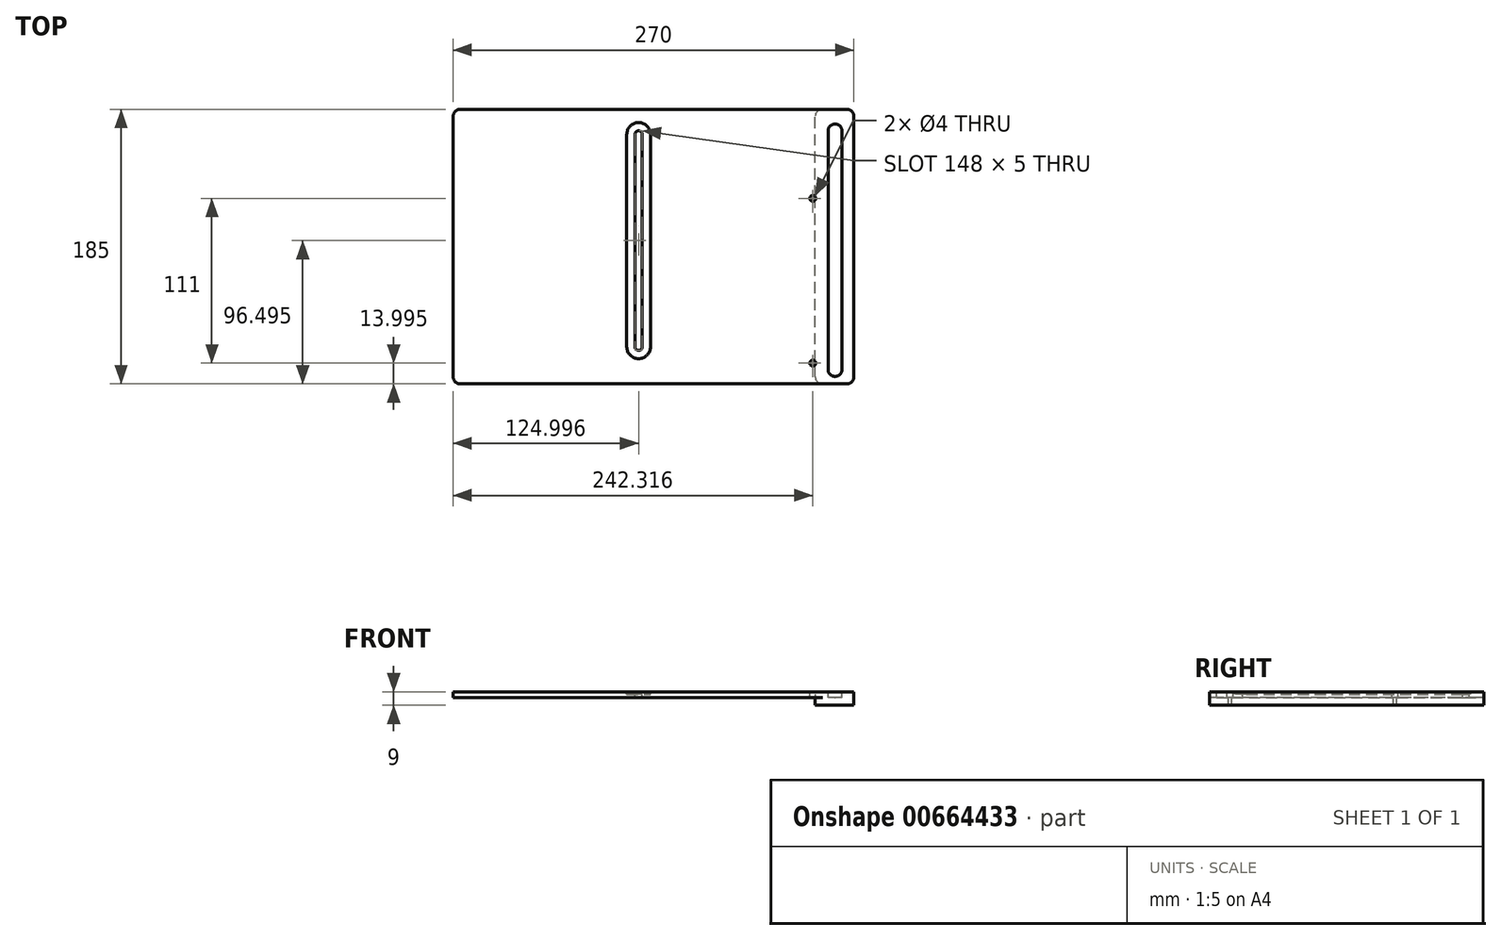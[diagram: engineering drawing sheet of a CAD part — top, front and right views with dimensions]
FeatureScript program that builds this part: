
annotation { "Feature Type Name" : "Feature", "Feature Type Description" : "" }
export const myFeature = defineFeature(function(context is Context, id is Id, definition is map)
    precondition{}
    {
        {
            var Q0;
            Q0=qCreatedBy(makeId("Top.planeOp"),FACE);
            var sketch = newSketch(context, id + "F0", { "sketchPlane" : qUnion([Q0])});
            skLineSegment(sketch, "E0.bottom", {"start": v(-79.13, 97.17) * mm, "end": v(170.87, 97.17) * mm});
            skLineSegment(sketch, "E0.top", {"start": v(-79.13, -87.83) * mm, "end": v(170.87, -87.83) * mm});
            skLineSegment(sketch, "E0.left", {"start": v(-79.13, 97.17) * mm, "end": v(-79.13, -87.83) * mm});
            skLineSegment(sketch, "E0.right", {"start": v(170.87, 97.17) * mm, "end": v(170.87, -87.83) * mm});
            skSolve(sketch);
        }
        {
            var Q0;
            Q0=makeQuery(id+"F0.imprint","IMPRINT",FACE,{"disambiguationData":[TD([[makeQuery(id+"F0.imprint","IMPRINT",EDGE,{"derivedFrom":sQuery(id+"F0.wireOp",EDGE,"E0.bottom")}),-1.0]])]});
            extrude(context, id + "F1", {"entities" : qUnion([Q0]), "depth" : 4 * mm, "offsetDistance" : 25 * mm});
        }
        {
            var Q0;
            Q0=makeQuery(id+"F1.opExtrude","CAP_FACE",FACE,{"disambiguationData":[OSD([sQuery(id+"F0.wireOp",EDGE,"E0.bottom"),sQuery(id+"F0.wireOp",EDGE,"E0.top"),sQuery(id+"F0.wireOp",EDGE,"E0.left"),sQuery(id+"F0.wireOp",EDGE,"E0.right")])],"isStart":false});
            var sketch = newSketch(context, id + "F2", { "sketchPlane" : qUnion([Q0])});
            skLineSegment(sketch, "E1", {"start": v(45.87, 97.17) * mm, "end": v(45.87, 72.17) * mm});
            skArc(sketch, "E2", {"start": v(53.87, 80.17) * mm, "mid": v(45.87, 88.17) * mm, "end": v(37.87, 80.17) * mm});
            skArc(sketch, "E3", {"start": v(37.87, -62.83) * mm, "mid": v(45.87, -70.83) * mm, "end": v(53.87, -62.83) * mm});
            skLineSegment(sketch, "E4", {"start": v(37.87, 80.17) * mm, "end": v(37.87, -62.83) * mm});
            skLineSegment(sketch, "E5", {"start": v(53.87, -62.83) * mm, "end": v(53.87, 80.17) * mm});
            skLineSegment(sketch, "E6.trimOffspring", {"start": v(45.87, -54.83) * mm, "end": v(45.87, -87.83) * mm});
            skSolve(sketch);
        }
        {
            var Q0;
            {var subQ3=sQuery(id+"F2.wireOp",EDGE,"E4");Q0=makeQuery(id+"F2.imprint","IMPRINT",FACE,{"disambiguationData":[TD([[makeQuery(id+"F2.imprint","IMPRINT",EDGE,{"derivedFrom":subQ3}),1.0]])]});}
            var Q1;
            {var subQ0=sQuery(id+"F2.wireOp",EDGE,"E6.trimOffspring");var subQ1=sQuery(id+"F2.wireOp",EDGE,"E3");var subQ2=makeQuery(id+"F2.imprint","INTERSECT",VERTEX,{"disambiguationData":[OD(0.0)],"derivedFrom":[subQ1,subQ0]});Q1=makeQuery(id+"F2.imprint","IMPRINT",FACE,{"disambiguationData":[TD([[makeQuery(id+"F2.imprint","IMPRINT",EDGE,{"disambiguationData":[TD([[subQ2,-1.0]])],"derivedFrom":subQ1}),1.0]])]});}
            extrude(context, id + "F3", {"entities" : qUnion([Q0, Q1]), "operationType" : NewBodyOperationType.REMOVE, "oppositeDirection" : true, "depth" : 1.5 * mm, "offsetDistance" : 25 * mm});
        }
        {
            var Q0;
            Q0=makeQuery(id+"F3.boolean.opBoolean","COPY",FACE,{"derivedFrom":makeQuery(id+"F3.opExtrude","CAP_FACE",FACE,{"disambiguationData":[OSD([sQuery(id+"F2.wireOp",EDGE,"E2"),sQuery(id+"F2.wireOp",EDGE,"E3"),sQuery(id+"F2.wireOp",EDGE,"E4"),sQuery(id+"F2.wireOp",EDGE,"E5")])],"isStart":false})});
            var sketch = newSketch(context, id + "F4", { "sketchPlane" : qUnion([Q0])});
            skArc(sketch, "E7", {"start": v(48.37, 80.17) * mm, "mid": v(45.87, 82.67) * mm, "end": v(43.37, 80.17) * mm});
            skArc(sketch, "E8", {"start": v(43.37, -62.83) * mm, "mid": v(45.87, -65.33) * mm, "end": v(48.37, -62.83) * mm});
            skLineSegment(sketch, "E9", {"start": v(48.37, 80.17) * mm, "end": v(48.37, -62.83) * mm});
            skLineSegment(sketch, "E10", {"start": v(43.37, 80.17) * mm, "end": v(43.37, -62.83) * mm});
            skArc(sketch, "E11.0", {"start": v(53.37, 80.17) * mm, "mid": v(45.87, 87.67) * mm, "end": v(38.37, 80.17) * mm});
            skLineSegment(sketch, "E11.1", {"start": v(53.37, 80.17) * mm, "end": v(53.37, -62.83) * mm});
            skArc(sketch, "E11.2", {"start": v(38.37, -62.83) * mm, "mid": v(45.87, -70.33) * mm, "end": v(53.37, -62.83) * mm});
            skSolve(sketch);
        }
        {
            var Q0;
            {var subQ3=sQuery(id+"F4.wireOp",EDGE,"E8");Q0=makeQuery(id+"F4.imprint","IMPRINT",FACE,{"disambiguationData":[TD([[makeQuery(id+"F4.imprint","IMPRINT",EDGE,{"derivedFrom":subQ3}),1.0]])]});}
            extrude(context, id + "F5", {"entities" : qUnion([Q0]), "operationType" : NewBodyOperationType.REMOVE, "oppositeDirection" : true, "depth" : 5 * mm, "offsetDistance" : 25 * mm});
        }
        {
            var Q0;
            Q0=makeQuery(id+"F1.opExtrude","CAP_FACE",FACE,{"disambiguationData":[OSD([sQuery(id+"F0.wireOp",EDGE,"E0.bottom"),sQuery(id+"F0.wireOp",EDGE,"E0.top"),sQuery(id+"F0.wireOp",EDGE,"E0.left"),sQuery(id+"F0.wireOp",EDGE,"E0.right")])],"isStart":false});
            var sketch = newSketch(context, id + "F6", { "sketchPlane" : qUnion([Q0])});
            skLineSegment(sketch, "E12", {"start": v(170.87, 37.17) * mm, "end": v(163.19, 37.17) * mm});
            skCircle(sketch, "E13", {"center": v(163.19, 37.17) * mm, "radius": 2 * mm});
            skCircle(sketch, "E14", {"center": v(163.19, -73.83) * mm, "radius": 2 * mm});
            skSolve(sketch);
        }
        {
            var Q0;
            Q0=makeQuery(id+"F6.imprint","IMPRINT",FACE,{"disambiguationData":[TD([[makeQuery(id+"F6.imprint","IMPRINT",EDGE,{"derivedFrom":sQuery(id+"F6.wireOp",EDGE,"E13")}),1.0]])]});
            var Q1;
            Q1=makeQuery(id+"F6.imprint","IMPRINT",FACE,{"disambiguationData":[TD([[makeQuery(id+"F6.imprint","IMPRINT",EDGE,{"derivedFrom":sQuery(id+"F6.wireOp",EDGE,"E14")}),1.0]])]});
            extrude(context, id + "F7", {"entities" : qUnion([Q0, Q1]), "operationType" : NewBodyOperationType.REMOVE, "oppositeDirection" : true, "depth" : 25 * mm, "offsetDistance" : 25 * mm});
        }
        {
            var Q0;
            Q0=makeQuery(id+"F1.opExtrude","SWEPT_FACE",FACE,{"disambiguationData":[OSD([sQuery(id+"F0.wireOp",EDGE,"E0.right")])]});
            extrude(context, id + "F8", {"entities" : qUnion([Q0]), "operationType" : NewBodyOperationType.ADD, "depth" : 20 * mm, "offsetDistance" : 25 * mm});
        }
        {
            var Q0;
            {var subQ0=sQuery(id+"F0.wireOp",EDGE,"E0.right");Q0=makeQuery(id+"F8.boolean.opBoolean","MERGE",FACE,{"derivedFrom":[makeQuery(id+"F1.opExtrude","CAP_FACE",FACE,{"disambiguationData":[OSD([sQuery(id+"F0.wireOp",EDGE,"E0.bottom"),sQuery(id+"F0.wireOp",EDGE,"E0.top"),sQuery(id+"F0.wireOp",EDGE,"E0.left"),subQ0])],"isStart":false}),makeQuery(id+"F8.opExtrude","SWEPT_FACE",FACE,{"disambiguationData":[OSD([subQ0]),TDD([makeQuery(id+"F1.opExtrude","CAP_EDGE",EDGE,{"disambiguationData":[OSD([subQ0])],"isStart":false})])]})]});}
            var sketch = newSketch(context, id + "F9", { "sketchPlane" : qUnion([Q0])});
            skLineSegment(sketch, "E15.bottom", {"start": v(178.07, 87.17) * mm, "end": v(178.37, 87.17) * mm});
            skLineSegment(sketch, "E15.top", {"start": v(178.07, -82.83) * mm, "end": v(178.37, -82.83) * mm});
            skLineSegment(sketch, "E15.left", {"start": v(173.57, 82.67) * mm, "end": v(173.57, -78.33) * mm});
            skLineSegment(sketch, "E15.right", {"start": v(182.87, 82.67) * mm, "end": v(182.87, -78.33) * mm});
            skPoint(sketch, "E16.visualSharp", {"position": v(182.87, 87.17) * mm});
            skArc(sketch, "E16.filletArc", {"start": v(182.87, 82.67) * mm, "mid": v(181.55, 85.85) * mm, "end": v(178.37, 87.17) * mm});
            skPoint(sketch, "E17.visualSharp", {"position": v(173.57, 87.17) * mm});
            skArc(sketch, "E17.filletArc", {"start": v(178.07, 87.17) * mm, "mid": v(174.88, 85.85) * mm, "end": v(173.57, 82.67) * mm});
            skPoint(sketch, "E18.visualSharp", {"position": v(182.87, -82.83) * mm});
            skArc(sketch, "E18.filletArc", {"start": v(178.37, -82.83) * mm, "mid": v(181.55, -81.52) * mm, "end": v(182.87, -78.33) * mm});
            skPoint(sketch, "E19.visualSharp", {"position": v(173.57, -82.83) * mm});
            skArc(sketch, "E19.filletArc", {"start": v(173.57, -78.33) * mm, "mid": v(174.88, -81.52) * mm, "end": v(178.07, -82.83) * mm});
            skSolve(sketch);
        }
        {
            var Q0;
            Q0=makeQuery(id+"F9.imprint","IMPRINT",FACE,{"disambiguationData":[TD([[makeQuery(id+"F9.imprint","IMPRINT",EDGE,{"derivedFrom":sQuery(id+"F9.wireOp",EDGE,"E15.bottom")}),-1.0]])]});
            extrude(context, id + "F10", {"entities" : qUnion([Q0]), "operationType" : NewBodyOperationType.REMOVE, "endBound" : BoundingType.THROUGH_ALL, "oppositeDirection" : true, "depth" : 25 * mm, "offsetDistance" : 25 * mm});
        }
        {
            var Q0;
            {var subQ0=sQuery(id+"F0.wireOp",EDGE,"E0.right");Q0=makeQuery(id+"F8.boolean.opBoolean","MERGE",FACE,{"derivedFrom":[makeQuery(id+"F1.opExtrude","CAP_FACE",FACE,{"disambiguationData":[OSD([sQuery(id+"F0.wireOp",EDGE,"E0.bottom"),sQuery(id+"F0.wireOp",EDGE,"E0.top"),sQuery(id+"F0.wireOp",EDGE,"E0.left"),subQ0])],"isStart":true}),makeQuery(id+"F8.opExtrude","SWEPT_FACE",FACE,{"disambiguationData":[OSD([subQ0]),TDD([makeQuery(id+"F1.opExtrude","CAP_EDGE",EDGE,{"disambiguationData":[OSD([subQ0])],"isStart":true})])]})]});}
            var sketch = newSketch(context, id + "F11", { "sketchPlane" : qUnion([Q0])});
            skLineSegment(sketch, "E20.bottom", {"start": v(190.87, 87.83) * mm, "end": v(164.82, 87.83) * mm});
            skLineSegment(sketch, "E20.top", {"start": v(190.87, -97.17) * mm, "end": v(164.82, -97.17) * mm});
            skLineSegment(sketch, "E20.left", {"start": v(190.87, 87.83) * mm, "end": v(190.87, -97.17) * mm});
            skLineSegment(sketch, "E20.right", {"start": v(164.82, 87.83) * mm, "end": v(164.82, -97.17) * mm});
            skSolve(sketch);
        }
        {
            var Q0;
            {var subQ0=sQuery(id+"F0.wireOp",EDGE,"E0.right");var subQ1=makeQuery(id+"F8.boolean.opBoolean","MERGE",FACE,{"derivedFrom":[makeQuery(id+"F1.opExtrude","CAP_FACE",FACE,{"disambiguationData":[OSD([sQuery(id+"F0.wireOp",EDGE,"E0.bottom"),sQuery(id+"F0.wireOp",EDGE,"E0.top"),sQuery(id+"F0.wireOp",EDGE,"E0.left"),subQ0])],"isStart":true}),makeQuery(id+"F8.opExtrude","SWEPT_FACE",FACE,{"disambiguationData":[OSD([subQ0]),TDD([makeQuery(id+"F1.opExtrude","CAP_EDGE",EDGE,{"disambiguationData":[OSD([subQ0])],"isStart":true})])]})]});Q0=makeQuery(id+"F11.imprint","IMPRINT",FACE,{"disambiguationData":[TD([[makeQuery(id+"F11.imprint","IMPRINT",EDGE,{"derivedFrom":makeQuery(id+"F10.boolean.opBoolean","INTERSECT",EDGE,{"derivedFrom":[subQ1,makeQuery(id+"F10.opExtrude","SWEPT_FACE",FACE,{"disambiguationData":[OSD([sQuery(id+"F9.wireOp",EDGE,"E15.bottom")])]})]})}),1.0]])]});}
            var Q1;
            Q1=makeQuery(id+"F11.imprint","IMPRINT",FACE,{"disambiguationData":[TD([[makeQuery(id+"F11.imprint","IMPRINT",EDGE,{"derivedFrom":sQuery(id+"F11.wireOp",EDGE,"E20.bottom")}),-1.0]])]});
            extrude(context, id + "F12", {"entities" : qUnion([Q0, Q1]), "operationType" : NewBodyOperationType.ADD, "depth" : 5 * mm, "offsetDistance" : 25 * mm});
        }
        {
            var Q0;
            Q0=makeQuery(id+"F12.boolean.opBoolean","MERGE",EDGE,{"derivedFrom":[makeQuery(id+"F8.opExtrude","CAP_EDGE",EDGE,{"disambiguationData":[OSD([sQuery(id+"F0.wireOp",EDGE,"E0.bottom"),sQuery(id+"F0.wireOp",EDGE,"E0.right")])],"isStart":false}),makeQuery(id+"F12.opExtrude","SWEPT_EDGE",EDGE,{"disambiguationData":[OSD([sQuery(id+"F11.wireOp",EDGE,"E20.top"),sQuery(id+"F11.wireOp",EDGE,"E20.left")])]})]});
            var Q1;
            Q1=makeQuery(id+"F1.opExtrude","SWEPT_EDGE",EDGE,{"disambiguationData":[OSD([sQuery(id+"F0.wireOp",EDGE,"E0.bottom"),sQuery(id+"F0.wireOp",EDGE,"E0.left")])]});
            var Q2;
            Q2=makeQuery(id+"F1.opExtrude","SWEPT_EDGE",EDGE,{"disambiguationData":[OSD([sQuery(id+"F0.wireOp",EDGE,"E0.top"),sQuery(id+"F0.wireOp",EDGE,"E0.left")])]});
            var Q3;
            Q3=makeQuery(id+"F12.boolean.opBoolean","MERGE",EDGE,{"derivedFrom":[makeQuery(id+"F8.opExtrude","CAP_EDGE",EDGE,{"disambiguationData":[OSD([sQuery(id+"F0.wireOp",EDGE,"E0.top"),sQuery(id+"F0.wireOp",EDGE,"E0.right")])],"isStart":false}),makeQuery(id+"F12.opExtrude","SWEPT_EDGE",EDGE,{"disambiguationData":[OSD([sQuery(id+"F11.wireOp",EDGE,"E20.bottom"),sQuery(id+"F11.wireOp",EDGE,"E20.left")])]})]});
            var Q4;
            Q4=makeQuery(id+"F12.opExtrude","SWEPT_EDGE",EDGE,{"disambiguationData":[OSD([sQuery(id+"F0.wireOp",EDGE,"E0.top"),sQuery(id+"F0.wireOp",EDGE,"E0.right"),sQuery(id+"F11.wireOp",EDGE,"E20.bottom"),sQuery(id+"F11.wireOp",EDGE,"E20.right")])]});
            var Q5;
            Q5=makeQuery(id+"F12.opExtrude","SWEPT_EDGE",EDGE,{"disambiguationData":[OSD([sQuery(id+"F0.wireOp",EDGE,"E0.bottom"),sQuery(id+"F0.wireOp",EDGE,"E0.right"),sQuery(id+"F11.wireOp",EDGE,"E20.top"),sQuery(id+"F11.wireOp",EDGE,"E20.right")])]});
            fillet(context, id + "F13", {"entities" : qUnion([Q0, Q1, Q2, Q3, Q4, Q5]), "radius" : 5 * mm, "tangentPropagation" : true, "allowEdgeOverflow" : false});
        }
    });
